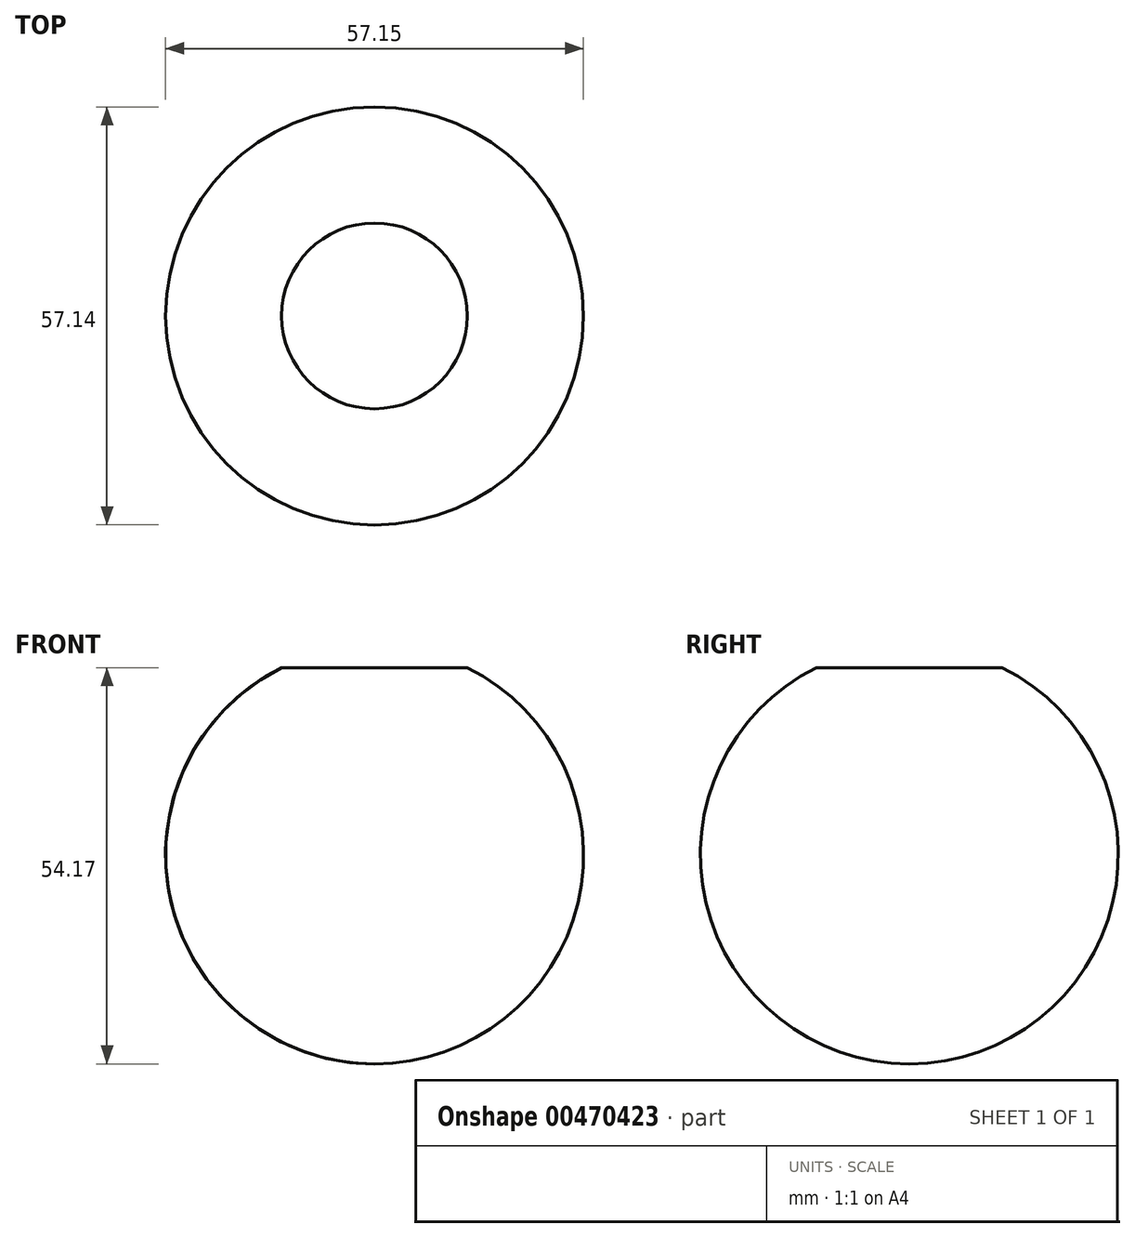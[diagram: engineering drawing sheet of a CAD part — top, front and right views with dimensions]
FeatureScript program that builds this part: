
annotation { "Feature Type Name" : "Feature", "Feature Type Description" : "" }
export const myFeature = defineFeature(function(context is Context, id is Id, definition is map)
    precondition{}
    {
        {
            var Q0;
            Q0=qCreatedBy(makeId("Front.planeOp"),FACE);
            var sketch = newSketch(context, id + "F0", { "sketchPlane" : qUnion([Q0])});
            skCircle(sketch, "E0", {"center": v(0, 0) * mm, "radius": 28.58 * mm});
            skLineSegment(sketch, "E1", {"start": v(0, 0) * mm, "end": v(28.57, 0) * mm});
            skLineSegment(sketch, "E2", {"start": v(28.57, 0) * mm, "end": v(0, 0) * mm});
            skLineSegment(sketch, "E3", {"start": v(-28.57, 0) * mm, "end": v(0, 0) * mm});
            skLineSegment(sketch, "E4", {"start": v(0, -28.57) * mm, "end": v(0, 0) * mm});
            skLineSegment(sketch, "E5", {"start": v(0, 28.57) * mm, "end": v(0, 0) * mm});
            skLineSegment(sketch, "E6.bottom", {"start": v(12.7, -25.6) * mm, "end": v(-12.7, -25.6) * mm});
            skLineSegment(sketch, "E6.top", {"start": v(12.7, 25.6) * mm, "end": v(-12.7, 25.6) * mm});
            skLineSegment(sketch, "E6.left", {"start": v(12.7, -25.6) * mm, "end": v(12.7, 25.6) * mm});
            skLineSegment(sketch, "E6.right", {"start": v(-12.7, -25.6) * mm, "end": v(-12.7, 25.6) * mm});
            skSolve(sketch);
        }
        {
            var Q0;
            Q0=qCreatedBy(makeId("Top.planeOp"),FACE);
            var sketch = newSketch(context, id + "F1", { "sketchPlane" : qUnion([Q0])});
            skCircle(sketch, "E7", {"center": v(0, 0) * mm, "radius": 28.58 * mm});
            skLineSegment(sketch, "E8.bottom", {"start": v(-12.7, -12.7) * mm, "end": v(12.7, -12.7) * mm});
            skLineSegment(sketch, "E8.top", {"start": v(-12.7, 12.7) * mm, "end": v(12.7, 12.7) * mm});
            skLineSegment(sketch, "E8.left", {"start": v(-12.7, 12.7) * mm, "end": v(-12.7, -12.7) * mm});
            skLineSegment(sketch, "E8.right", {"start": v(12.7, 12.7) * mm, "end": v(12.7, -12.7) * mm});
            skSolve(sketch);
        }
        {
            var Q0;
            {var subQ0=sQuery(id+"F0.wireOp",EDGE,"E3");var subQ1=sQuery(id+"F0.wireOp",EDGE,"E0");var subQ2=makeQuery(id+"F0.imprint","INTERSECT",VERTEX,{"derivedFrom":[subQ1,subQ0]});Q0=makeQuery(id+"F0.imprint","IMPRINT",FACE,{"disambiguationData":[TD([[makeQuery(id+"F0.imprint","IMPRINT",EDGE,{"disambiguationData":[TD([[subQ2,-1.0]])],"derivedFrom":subQ0}),1.0]])]});}
            var sketch = newSketch(context, id + "F2", { "sketchPlane" : qUnion([Q0])});
            skLineSegment(sketch, "E9", {"start": v(-12.7, 0) * mm, "end": v(-12.7, 25.6) * mm});
            skLineSegment(sketch, "E10", {"start": v(-12.7, 0) * mm, "end": v(0, 0) * mm});
            skLineSegment(sketch, "E11", {"start": v(0, 25.6) * mm, "end": v(0, 0) * mm});
            skLineSegment(sketch, "E12", {"start": v(0, 25.6) * mm, "end": v(-12.7, 25.6) * mm});
            skSolve(sketch);
        }
        {
            var Q0;
            {var subQ0=sQuery(id+"F0.wireOp",EDGE,"E3");var subQ1=sQuery(id+"F0.wireOp",EDGE,"E0");var subQ2=makeQuery(id+"F0.imprint","INTERSECT",VERTEX,{"derivedFrom":[subQ1,subQ0]});Q0=makeQuery(id+"F0.imprint","IMPRINT",FACE,{"disambiguationData":[TD([[makeQuery(id+"F0.imprint","IMPRINT",EDGE,{"disambiguationData":[TD([[subQ2,-1.0]])],"derivedFrom":subQ0}),1.0]])]});}
            var Q1;
            {var subQ0=sQuery(id+"F0.wireOp",EDGE,"E5");var subQ5=sQuery(id+"F0.wireOp",EDGE,"E6.top");var subQ6=makeQuery(id+"F0.imprint","INTERSECT",VERTEX,{"derivedFrom":[subQ0,subQ5]});Q1=makeQuery(id+"F0.imprint","IMPRINT",FACE,{"disambiguationData":[TD([[makeQuery(id+"F0.imprint","IMPRINT",EDGE,{"disambiguationData":[TD([[subQ6,-1.0]])],"derivedFrom":subQ5}),1.0]])]});}
            var Q2;
            Q2=sQuery(id+"F2.wireOp",EDGE,"E11");
            revolve(context, id + "F3", {"entities" : qUnion([Q0, Q1]), "axis" : qUnion([Q2]), "revolveType" : RevolveType.FULL});
        }
        {
            var Q0;
            Q0 = qSketchRegion(id + "F1", true);
            var sketch = newSketch(context, id + "F4", { "sketchPlane" : qUnion([Q0])});
            skSolve(sketch);
        }
        {
            var Q0;
            Q0=makeQuery(id+"F4.imprint","IMPRINT",FACE,{"disambiguationData":[TD([[makeQuery(id+"F4.imprint","IMPRINT",EDGE,{"derivedFrom":makeQuery(id+"F1.imprint","IMPRINT",EDGE,{"derivedFrom":sQuery(id+"F1.wireOp",EDGE,"E7")})}),1.0]])]});
            var Q1;
            Q1=makeQuery(id+"F4.imprint","IMPRINT",FACE,{"disambiguationData":[TD([[makeQuery(id+"F4.imprint","IMPRINT",EDGE,{"derivedFrom":makeQuery(id+"F1.imprint","IMPRINT",EDGE,{"derivedFrom":sQuery(id+"F1.wireOp",EDGE,"E8.bottom")})}),1.0]])]});
            var Q2;
            Q2=sQuery(id+"F1.wireOp",EDGE,"E7");
            extrude(context, id + "F5", {"entities" : qUnion([Q0, Q1]), "operationType" : NewBodyOperationType.ADD, "surfaceEntities" : qUnion([Q2]), "oppositeDirection" : true, "depth" : 28.57 * mm});
        }
        {
            var Q0;
            Q0=makeQuery(id+"F5.opExtrude","CAP_EDGE",EDGE,{"disambiguationData":[OSD([sQuery(id+"F1.wireOp",EDGE,"E7")])],"isStart":false});
            fillet(context, id + "F6", {"entities" : qUnion([Q0]), "radius" : 28.57 * mm, "tangentPropagation" : true, "allowEdgeOverflow" : false});
        }
    });
